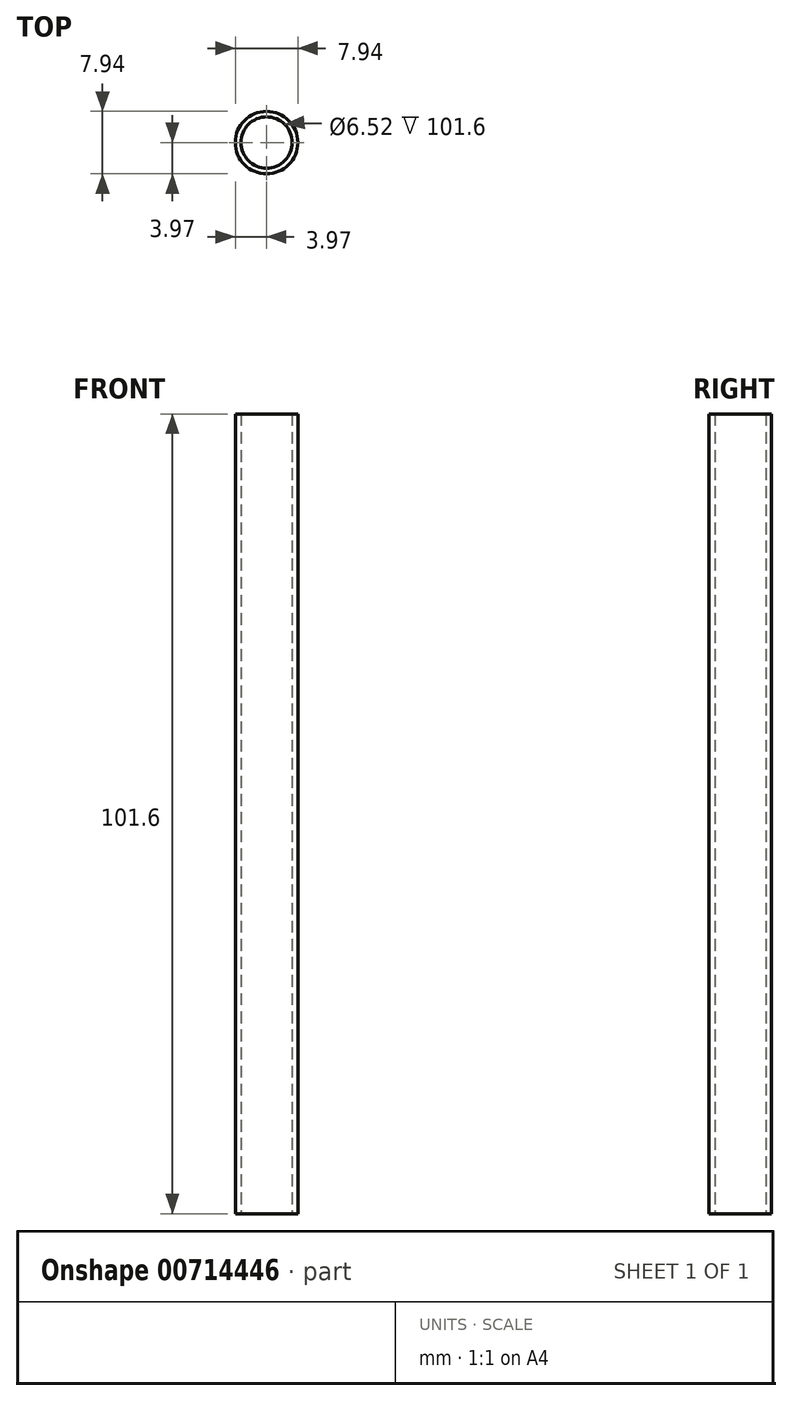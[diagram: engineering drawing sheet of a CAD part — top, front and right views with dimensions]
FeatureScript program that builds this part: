
annotation { "Feature Type Name" : "Feature", "Feature Type Description" : "" }
export const myFeature = defineFeature(function(context is Context, id is Id, definition is map)
    precondition{}
    {
        {
            var Q0;
            Q0=qCreatedBy(makeId("Top.planeOp"),FACE);
            var sketch = newSketch(context, id + "F0", { "sketchPlane" : qUnion([Q0])});
            skCircle(sketch, "E0", {"center": v(0, 0) * mm, "radius": 3.26 * mm});
            skCircle(sketch, "E1", {"center": v(0, 0) * mm, "radius": 3.97 * mm});
            skSolve(sketch);
        }
        {
            var Q0;
            Q0=makeQuery(id+"F0.imprint","IMPRINT",FACE,{"disambiguationData":[TD([[makeQuery(id+"F0.imprint","IMPRINT",EDGE,{"derivedFrom":sQuery(id+"F0.wireOp",EDGE,"E0")}),-1.0]])]});
            extrude(context, id + "F1", {"entities" : qUnion([Q0]), "depth" : 101.6 * mm});
        }
    });
